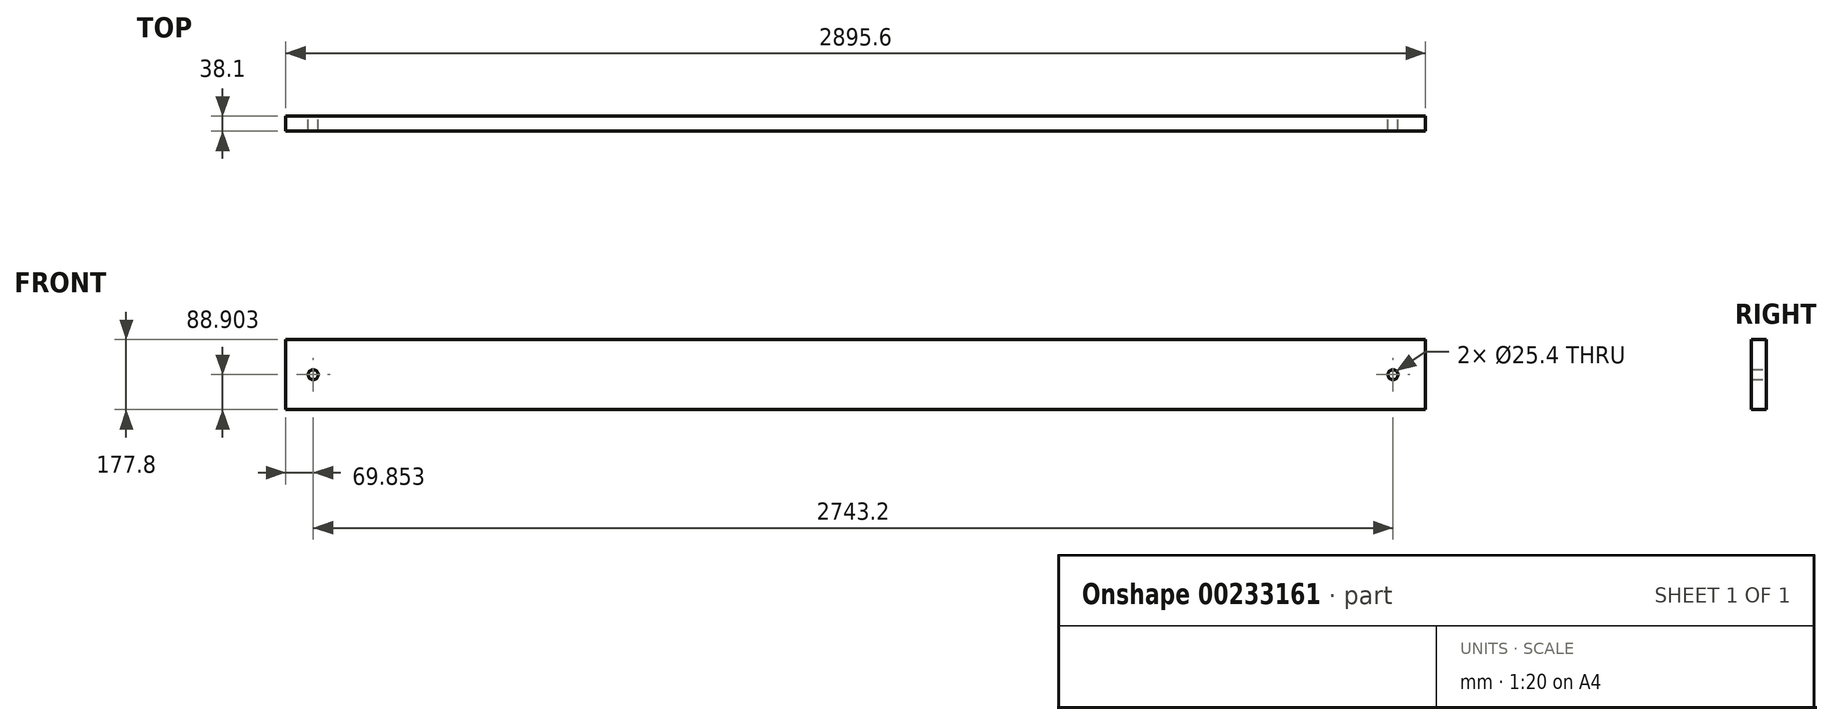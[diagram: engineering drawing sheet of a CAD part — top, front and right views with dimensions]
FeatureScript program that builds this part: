
annotation { "Feature Type Name" : "Feature", "Feature Type Description" : "" }
export const myFeature = defineFeature(function(context is Context, id is Id, definition is map)
    precondition{}
    {
        {
            var Q0;
            Q0=qCreatedBy(makeId("Front.planeOp"),FACE);
            var sketch = newSketch(context, id + "F0", { "sketchPlane" : qUnion([Q0])});
            skLineSegment(sketch, "E0.bottom", {"start": v(-2857.95, 162.46) * mm, "end": v(37.65, 162.46) * mm});
            skLineSegment(sketch, "E0.top", {"start": v(-2857.95, -15.34) * mm, "end": v(37.65, -15.34) * mm});
            skLineSegment(sketch, "E0.left", {"start": v(-2857.95, 162.46) * mm, "end": v(-2857.95, -15.34) * mm});
            skLineSegment(sketch, "E0.right", {"start": v(37.65, 162.46) * mm, "end": v(37.65, -15.34) * mm});
            skCircle(sketch, "E1", {"center": v(-2788.1, 73.56) * mm, "radius": 12.7 * mm});
            skCircle(sketch, "E2", {"center": v(-44.9, 73.56) * mm, "radius": 12.7 * mm});
            skSolve(sketch);
        }
        {
            var Q0;
            Q0=makeQuery(id+"F0.imprint","IMPRINT",FACE,{"disambiguationData":[TD([[makeQuery(id+"F0.imprint","IMPRINT",EDGE,{"derivedFrom":sQuery(id+"F0.wireOp",EDGE,"E0.bottom")}),-1.0]])]});
            extrude(context, id + "F1", {"entities" : qUnion([Q0]), "depth" : 38.1 * mm});
        }
    });
